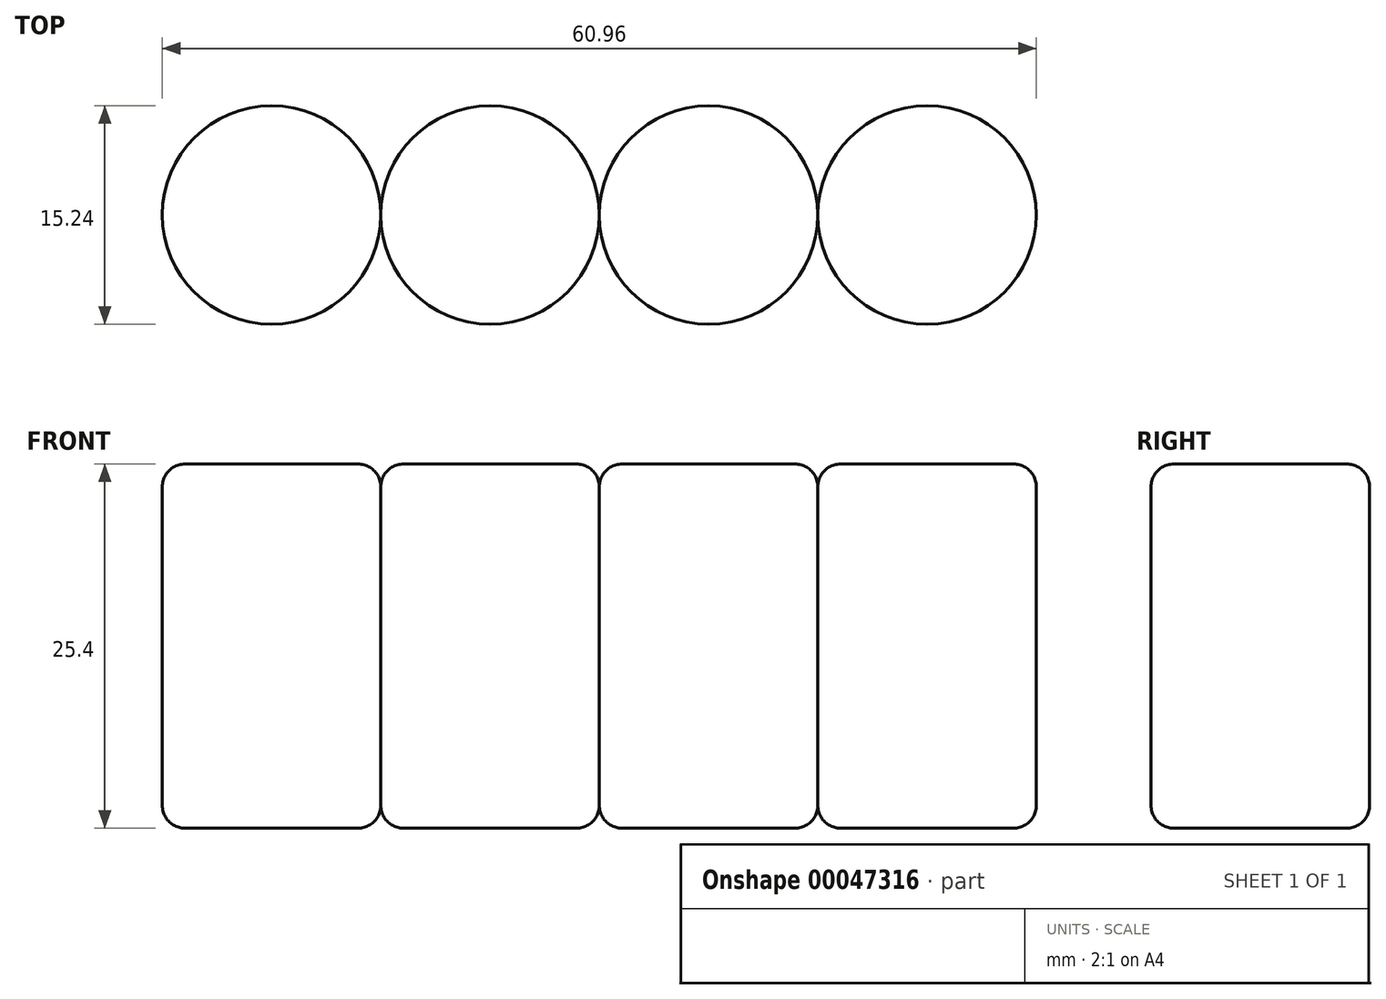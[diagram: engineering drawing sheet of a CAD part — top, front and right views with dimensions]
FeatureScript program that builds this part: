
annotation { "Feature Type Name" : "Feature", "Feature Type Description" : "" }
export const myFeature = defineFeature(function(context is Context, id is Id, definition is map)
    precondition{}
    {
        {
            var Q0;
            Q0=qCreatedBy(makeId("Top.planeOp"),FACE);
            var sketch = newSketch(context, id + "F0", { "sketchPlane" : qUnion([Q0])});
            skCircle(sketch, "E0", {"center": v(0, 0) * mm, "radius": 7.62 * mm});
            skCircle(sketch, "E1", {"center": v(15.24, 0) * mm, "radius": 7.62 * mm});
            skCircle(sketch, "E2", {"center": v(30.48, 0) * mm, "radius": 7.62 * mm});
            skCircle(sketch, "E3", {"center": v(-15.24, 0) * mm, "radius": 7.62 * mm});
            skSolve(sketch);
        }
        {
            var Q0;
            Q0=makeQuery(id+"F0.imprint","IMPRINT",FACE,{"disambiguationData":[TD([[makeQuery(id+"F0.imprint","IMPRINT",EDGE,{"derivedFrom":sQuery(id+"F0.wireOp",EDGE,"E3")}),1.0]])]});
            var Q1;
            {var subQ0=sQuery(id+"F0.wireOp",EDGE,"E0");var subQ1=makeQuery(id+"F0.imprint","INTERSECT",VERTEX,{"derivedFrom":[subQ0,sQuery(id+"F0.wireOp",EDGE,"E1")]});Q1=makeQuery(id+"F0.imprint","IMPRINT",FACE,{"disambiguationData":[TD([[makeQuery(id+"F0.imprint","IMPRINT",EDGE,{"disambiguationData":[TD([[subQ1,-1.0]])],"derivedFrom":subQ0}),1.0]])]});}
            var Q2;
            {var subQ0=sQuery(id+"F0.wireOp",EDGE,"E1");var subQ1=makeQuery(id+"F0.imprint","INTERSECT",VERTEX,{"derivedFrom":[sQuery(id+"F0.wireOp",EDGE,"E0"),subQ0]});Q2=makeQuery(id+"F0.imprint","IMPRINT",FACE,{"disambiguationData":[TD([[makeQuery(id+"F0.imprint","IMPRINT",EDGE,{"disambiguationData":[TD([[subQ1,1.0]])],"derivedFrom":subQ0}),1.0]])]});}
            var Q3;
            Q3=makeQuery(id+"F0.imprint","IMPRINT",FACE,{"disambiguationData":[TD([[makeQuery(id+"F0.imprint","IMPRINT",EDGE,{"derivedFrom":sQuery(id+"F0.wireOp",EDGE,"E2")}),1.0]])]});
            extrude(context, id + "F1", {"entities" : qUnion([Q0, Q1, Q2, Q3]), "oppositeDirection" : true, "depth" : 25.4 * mm});
        }
        {
            var Q0;
            Q0=makeQuery(id+"F1.opExtrude","CAP_EDGE",EDGE,{"disambiguationData":[OSD([sQuery(id+"F0.wireOp",EDGE,"E3")])],"isStart":false});
            var Q1;
            Q1=makeQuery(id+"F1.opExtrude","CAP_EDGE",EDGE,{"disambiguationData":[OSD([sQuery(id+"F0.wireOp",EDGE,"E0")])],"isStart":false});
            var Q2;
            Q2=makeQuery(id+"F1.opExtrude","CAP_EDGE",EDGE,{"disambiguationData":[OSD([sQuery(id+"F0.wireOp",EDGE,"E1")])],"isStart":false});
            var Q3;
            Q3=makeQuery(id+"F1.opExtrude","CAP_EDGE",EDGE,{"disambiguationData":[OSD([sQuery(id+"F0.wireOp",EDGE,"E2")])],"isStart":false});
            var Q4;
            Q4=makeQuery(id+"F1.opExtrude","CAP_EDGE",EDGE,{"disambiguationData":[OSD([sQuery(id+"F0.wireOp",EDGE,"E1")])],"isStart":true});
            var Q5;
            Q5=makeQuery(id+"F1.opExtrude","SWEPT_FACE",FACE,{"disambiguationData":[OSD([sQuery(id+"F0.wireOp",EDGE,"E2")])]});
            var Q6;
            Q6=makeQuery(id+"F1.opExtrude","SWEPT_FACE",FACE,{"disambiguationData":[OSD([sQuery(id+"F0.wireOp",EDGE,"E0")])]});
            var Q7;
            Q7=makeQuery(id+"F1.opExtrude","CAP_EDGE",EDGE,{"disambiguationData":[OSD([sQuery(id+"F0.wireOp",EDGE,"E3")])],"isStart":true});
            fillet(context, id + "F2", {"entities" : qUnion([Q0, Q1, Q2, Q3, Q4, Q5, Q6, Q7]), "radius" : 1.59 * mm, "tangentPropagation" : true, "allowEdgeOverflow" : false});
        }
    });
